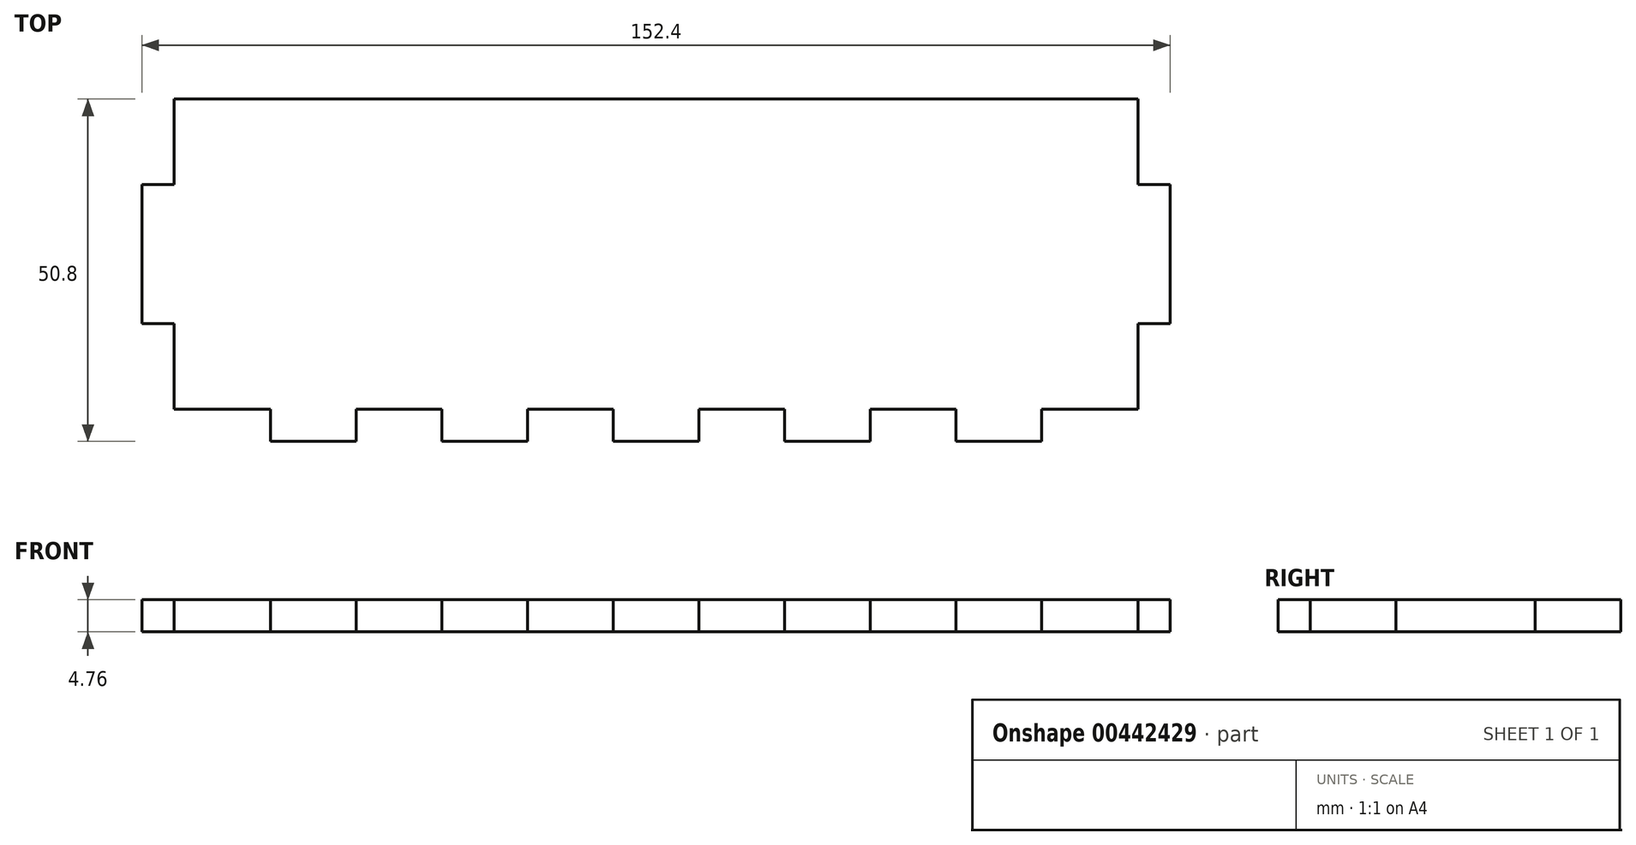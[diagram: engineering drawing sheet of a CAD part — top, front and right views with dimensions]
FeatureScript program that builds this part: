
annotation { "Feature Type Name" : "Feature", "Feature Type Description" : "" }
export const myFeature = defineFeature(function(context is Context, id is Id, definition is map)
    precondition{}
    {
        {
            var Q0;
            Q0=qCreatedBy(makeId("Top.planeOp"),FACE);
            var sketch = newSketch(context, id + "F0", { "sketchPlane" : qUnion([Q0])});
            skLineSegment(sketch, "E0.bottom", {"start": v(-76.2, 25.4) * mm, "end": v(76.2, 25.4) * mm});
            skLineSegment(sketch, "E0.top", {"start": v(-76.2, -25.4) * mm, "end": v(76.2, -25.4) * mm});
            skLineSegment(sketch, "E0.left", {"start": v(-76.2, 25.4) * mm, "end": v(-76.2, -25.4) * mm});
            skLineSegment(sketch, "E0.right", {"start": v(76.2, 25.4) * mm, "end": v(76.2, -25.4) * mm});
            skPoint(sketch, "E0.middle", {"position": v(0, 0) * mm});
            skSolve(sketch);
        }
        {
            var Q0;
            Q0 = qSketchRegion(id + "F0", true);
            extrude(context, id + "F1", {"entities" : qUnion([Q0]), "depth" : 4.76 * mm});
        }
        {
            var Q0;
            Q0=makeQuery(id+"F1.opExtrude","CAP_FACE",FACE,{"disambiguationData":[OSD([sQuery(id+"F0.wireOp",EDGE,"E0.bottom"),sQuery(id+"F0.wireOp",EDGE,"E0.top"),sQuery(id+"F0.wireOp",EDGE,"E0.left"),sQuery(id+"F0.wireOp",EDGE,"E0.right")])],"isStart":false});
            var sketch = newSketch(context, id + "F2", { "sketchPlane" : qUnion([Q0])});
            skLineSegment(sketch, "E1", {"start": v(-76.2, -20.64) * mm, "end": v(19.05, -20.64) * mm, "construction": true});
            skLineSegment(sketch, "E2", {"start": v(-57.15, -25.4) * mm, "end": v(-57.15, -20.64) * mm});
            skLineSegment(sketch, "E3", {"start": v(-57.15, -25.4) * mm, "end": v(-76.2, -25.4) * mm});
            skLineSegment(sketch, "E4", {"start": v(-76.2, -25.4) * mm, "end": v(-76.2, -20.64) * mm});
            skLineSegment(sketch, "E5", {"start": v(-57.15, -20.64) * mm, "end": v(-76.2, -20.64) * mm});
            skLineSegment(sketch, "E6", {"start": v(-44.45, -25.4) * mm, "end": v(-44.45, -20.64) * mm});
            skLineSegment(sketch, "E7.1.0.0", {"start": v(-31.75, -25.4) * mm, "end": v(-31.75, -20.64) * mm});
            skLineSegment(sketch, "E7.2.0.0", {"start": v(-19.05, -25.4) * mm, "end": v(-19.05, -20.64) * mm});
            skLineSegment(sketch, "E7.3.0.0", {"start": v(-6.35, -25.4) * mm, "end": v(-6.35, -20.64) * mm});
            skLineSegment(sketch, "E7.4.0.0", {"start": v(6.35, -25.4) * mm, "end": v(6.35, -20.64) * mm});
            skLineSegment(sketch, "E7.direction1", {"start": v(-44.45, -25.4) * mm, "end": v(-31.75, -25.4) * mm, "construction": true});
            skLineSegment(sketch, "E8", {"start": v(-44.45, -20.64) * mm, "end": v(-31.75, -20.64) * mm});
            skLineSegment(sketch, "E9", {"start": v(-31.75, -25.4) * mm, "end": v(-44.45, -25.4) * mm});
            skLineSegment(sketch, "E10", {"start": v(-19.05, -20.64) * mm, "end": v(-6.35, -20.64) * mm});
            skLineSegment(sketch, "E11", {"start": v(-6.35, -25.4) * mm, "end": v(-19.05, -25.4) * mm});
            skLineSegment(sketch, "E12", {"start": v(6.35, -20.64) * mm, "end": v(19.05, -20.64) * mm});
            skLineSegment(sketch, "E13", {"start": v(76.2, -25.4) * mm, "end": v(57.15, -25.4) * mm});
            skLineSegment(sketch, "E14", {"start": v(76.2, -25.4) * mm, "end": v(76.2, -20.64) * mm});
            skLineSegment(sketch, "E15.0.5.0", {"start": v(19.05, -25.4) * mm, "end": v(19.05, -20.64) * mm});
            skLineSegment(sketch, "E15.0.6.0", {"start": v(31.75, -25.4) * mm, "end": v(31.75, -20.64) * mm});
            skLineSegment(sketch, "E15.0.7.0", {"start": v(44.45, -25.4) * mm, "end": v(44.45, -20.64) * mm});
            skLineSegment(sketch, "E16.0.8.0", {"start": v(57.15, -25.4) * mm, "end": v(57.15, -20.64) * mm});
            skLineSegment(sketch, "E17", {"start": v(31.75, -20.64) * mm, "end": v(44.45, -20.64) * mm});
            skLineSegment(sketch, "E18", {"start": v(57.15, -20.64) * mm, "end": v(76.2, -20.64) * mm});
            skLineSegment(sketch, "E19.trimOffspring", {"start": v(31.75, -20.64) * mm, "end": v(44.45, -20.64) * mm, "construction": true});
            skLineSegment(sketch, "E20.trimOffspring", {"start": v(19.05, -25.4) * mm, "end": v(6.35, -25.4) * mm});
            skLineSegment(sketch, "E21.trimOffspring", {"start": v(44.45, -25.4) * mm, "end": v(31.75, -25.4) * mm});
            skSolve(sketch);
        }
        {
            var Q0;
            Q0 = qSketchRegion(id + "F2", true);
            extrude(context, id + "F3", {"entities" : qUnion([Q0]), "operationType" : NewBodyOperationType.REMOVE, "oppositeDirection" : true, "depth" : 25.4 * mm});
        }
        {
            var Q0;
            Q0=makeQuery(id+"F1.opExtrude","CAP_FACE",FACE,{"disambiguationData":[OSD([sQuery(id+"F0.wireOp",EDGE,"E0.bottom"),sQuery(id+"F0.wireOp",EDGE,"E0.top"),sQuery(id+"F0.wireOp",EDGE,"E0.left"),sQuery(id+"F0.wireOp",EDGE,"E0.right")])],"isStart":false});
            var sketch = newSketch(context, id + "F4", { "sketchPlane" : qUnion([Q0])});
            skLineSegment(sketch, "E22", {"start": v(0, 0) * mm, "end": v(0, 4.13) * mm, "construction": true});
            skLineSegment(sketch, "E23", {"start": v(-76.2, 25.4) * mm, "end": v(-76.2, 12.7) * mm});
            skLineSegment(sketch, "E24", {"start": v(-76.2, 12.7) * mm, "end": v(-71.44, 12.7) * mm});
            skLineSegment(sketch, "E25", {"start": v(-71.44, 12.7) * mm, "end": v(-71.44, 25.4) * mm});
            skLineSegment(sketch, "E26", {"start": v(-71.44, 25.4) * mm, "end": v(-76.2, 25.4) * mm});
            skLineSegment(sketch, "E27", {"start": v(-76.2, -20.64) * mm, "end": v(-76.2, -7.94) * mm});
            skLineSegment(sketch, "E28", {"start": v(-76.2, -7.94) * mm, "end": v(-71.44, -7.94) * mm});
            skLineSegment(sketch, "E29", {"start": v(-71.44, -7.94) * mm, "end": v(-71.44, -20.64) * mm});
            skLineSegment(sketch, "E30", {"start": v(-71.44, -20.64) * mm, "end": v(-76.2, -20.64) * mm});
            skLineSegment(sketch, "E31.MirrorCS", {"start": v(76.2, 25.4) * mm, "end": v(76.2, 12.7) * mm});
            skLineSegment(sketch, "E32.MirrorCS", {"start": v(71.44, 25.4) * mm, "end": v(76.2, 25.4) * mm});
            skLineSegment(sketch, "E33.MirrorCS", {"start": v(71.44, 12.7) * mm, "end": v(71.44, 25.4) * mm});
            skLineSegment(sketch, "E34.MirrorCS", {"start": v(76.2, 12.7) * mm, "end": v(71.44, 12.7) * mm});
            skLineSegment(sketch, "E35.MirrorCS", {"start": v(76.2, -20.64) * mm, "end": v(76.2, -7.94) * mm});
            skLineSegment(sketch, "E36.MirrorCS", {"start": v(76.2, -7.94) * mm, "end": v(71.44, -7.94) * mm});
            skLineSegment(sketch, "E37.MirrorCS", {"start": v(71.44, -7.94) * mm, "end": v(71.44, -20.64) * mm});
            skLineSegment(sketch, "E38.MirrorCS", {"start": v(71.44, -20.64) * mm, "end": v(76.2, -20.64) * mm});
            skSolve(sketch);
        }
        {
            var Q0;
            Q0 = qSketchRegion(id + "F4", true);
            extrude(context, id + "F5", {"entities" : qUnion([Q0]), "operationType" : NewBodyOperationType.REMOVE, "oppositeDirection" : true, "depth" : 25.4 * mm});
        }
    });
